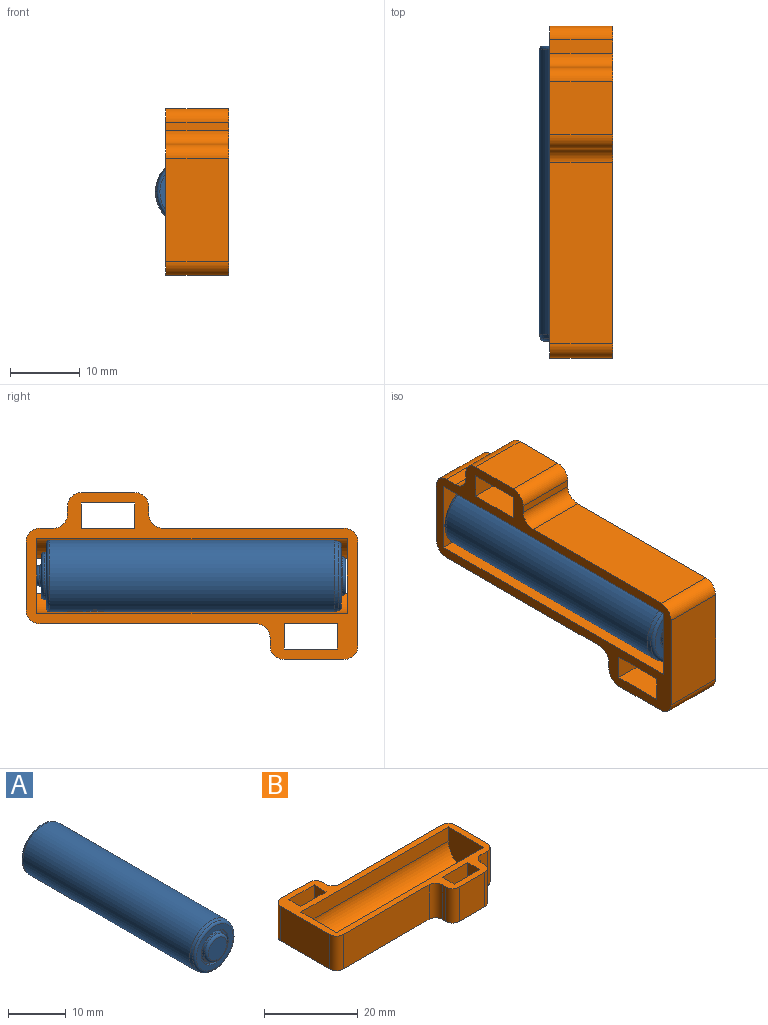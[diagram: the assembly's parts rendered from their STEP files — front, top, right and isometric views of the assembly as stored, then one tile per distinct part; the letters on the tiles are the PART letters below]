
ASSEMBLY  parts=2 mates=1
PART A: 180 faces, bbox 11.1x44.4x11.1 mm
  f0: cylinder r=4.92mm len=2.5mm, axis (0,-1,0), area 2.2mm2, adj f168,f169,f170,f171,f172,f173,f174,f175
  f1: cylinder r=4.92mm len=2.4mm, axis (0,-1,0), area 2.8mm2, adj f161,f162,f163,f164,f165,f166,f167
  f2: torus R=1.7mm, axis (0,1,0), area 3.1mm2, adj f12,f18
  f3: torus R=2.95mm, axis (0,-1,0), area 5.6mm2, adj f9,f21
  f4: torus R=1mm, axis (0,1,0), area 6.5mm2, adj f12,f19
  f5: torus R=4.62mm, axis (0,1,0), area 24.4mm2, adj f15,f16
  f6: torus R=2.9mm, axis (0,1,0), area 15.9mm2, adj f13,f18
  f7: torus R=4.48mm, axis (0,1,0), area 19.9mm2, adj f11,f20
  f8: torus R=2.25mm, axis (0,1,0), area 12.7mm2, adj f9,f22
  f9: cylinder r=2.75mm len=5.5mm, axis (0,-1,0), area 7.8mm2, adj f3,f8
  f10: cylinder r=3.35mm len=6.7mm, axis (0,-1,0), area 10.5mm2, adj f20,f21
  f11: cone r=5.12mm half-angle=14deg, axis (0,1,0), area 20.3mm2, adj f7,f15
  f12: cylinder r=1.5mm len=3mm, axis (0,-1,0), area 0.5mm2, adj f2,f4
  f13: cylinder r=3.4mm len=6.8mm, axis (0,1,0), area 9.6mm2, adj f6,f17
  f14: cylinder r=3.9mm len=7.8mm, axis (0,1,0), area 4.9mm2, adj f16,f17
  f15: cylinder r=5.12mm len=40.7mm, axis (0,-1,0), area 1276.3mm2, adj f5,f11,f23,f24,f25,f26,f27,f29
  f16: plane 9.25x9.25mm, normal (0,1,0), area 19.4mm2, adj f5,f14
  f17: plane 7.8x7.8mm, normal (0,1,0), area 11.5mm2, adj f13,f14
  f18: plane 5.8x5.8mm, normal (0,1,0), area 17.3mm2, adj f2,f6
  f19: plane 2x2mm, normal (0,1,0), area 3.1mm2, adj f4
  f20: plane 8.97x8.97mm, normal (0,-1,0), area 27.9mm2, adj f7,f10
  f21: plane 6.7x6.7mm, normal (0,-1,0), area 7.9mm2, adj f3,f10
  f22: plane 4.5x4.5mm, normal (0,-1,0), area 15.9mm2, adj f8
  f23: plane 0.64x0.19mm, normal (0.29,0,0.96), area 0.1mm2, adj f15,f24,f28,f29
  f24: bspline ~1.01x0.22mm, area 0.2mm2, adj f15,f23,f25,f28
  f25: bspline ~1.5x0.96mm, area 0.4mm2, adj f15,f24,f26,f28
  f26: bspline ~1.62x1.52mm, area 0.5mm2, adj f15,f25,f27,f28
  f27: plane 0.98x0.19mm, normal (0.32,0,-0.95), area 0.2mm2, adj f15,f26,f28,f29
  f28: cylinder r=4.92mm len=3mm, axis (0,-1,0), area 2.7mm2, adj f23,f24,f25,f26,f27,f29,f30,f31
  f29: plane 3.12x0.46mm, normal (0,-1,0), area 0.6mm2, adj f15,f23,f27,f28
  f30: bspline ~0.91x0.21mm, area 0.2mm2, adj f28,f31,f36,f37
  f31: bspline ~1.13x0.76mm, area 0.3mm2, adj f28,f30,f32,f37
  f32: bspline ~1.2x0.84mm, area 0.3mm2, adj f28,f31,f33,f37
  f33: bspline ~0.98x0.21mm, area 0.2mm2, adj f28,f32,f34,f37
  f34: plane 0.22x0.19mm, normal (-0.23,0,-0.97), area 0mm2, adj f28,f33,f35,f37
  f35: plane 2.5x0.37mm, normal (0,1,0), area 0.5mm2, adj f28,f34,f36,f37
  f36: plane 0.36x0.19mm, normal (-0.26,0,0.97), area 0.1mm2, adj f28,f30,f35,f37
  f37: cylinder r=5.12mm len=2.5mm, axis (0,-1,0), area 4.5mm2, adj f30,f31,f32,f33,f34,f35,f36
  f38: bspline ~0.99x0.69mm, area 0.3mm2, adj f15,f39,f50,f51
  f39: bspline ~1.32x0.99mm, area 0.4mm2, adj f15,f38,f40,f51
  f40: plane 1.9x0.41mm, normal (0,1,0), area 0.4mm2, adj f15,f39,f41,f51
  f41: plane 0.29x0.19mm, normal (0.29,0,0.96), area 0.1mm2, adj f15,f40,f42,f51
  f42: plane 1.88x0.41mm, normal (0,-1,0), area 0.4mm2, adj f15,f41,f43,f51
  f43: bspline ~0.5x0.26mm, area 0.1mm2, adj f15,f42,f44,f51
  f44: bspline ~0.69x0.56mm, area 0.2mm2, adj f15,f43,f45,f51
  f45: bspline ~0.74x0.62mm, area 0.2mm2, adj f15,f44,f46,f51
  f46: bspline ~0.43x0.25mm, area 0.1mm2, adj f15,f45,f47,f51
  f47: plane 1.88x0.41mm, normal (0,1,0), area 0.4mm2, adj f15,f46,f48,f51
  f48: plane 0.29x0.19mm, normal (0.29,0,0.96), area 0.1mm2, adj f15,f47,f49,f51
  f49: plane 1.9x0.41mm, normal (0,-1,0), area 0.4mm2, adj f15,f48,f50,f51
  f50: bspline ~0.68x0.29mm, area 0.1mm2, adj f15,f38,f49,f51
  f51: cylinder r=4.92mm len=3.08mm, axis (0,-1,0), area 2mm2, adj f38,f39,f40,f41,f42,f43,f44,f45
  f52: plane 1.44x0.45mm, normal (0,1,0), area 0.3mm2, adj f15,f53,f62,f63
  f53: plane 0.23x0.2mm, normal (0.04,0,-1), area 0mm2, adj f15,f52,f54,f63
  f54: bspline ~1.44x1.17mm, area 0.4mm2, adj f15,f53,f55,f63
  f55: plane 0.35x0.19mm, normal (0.32,0,-0.95), area 0.1mm2, adj f15,f54,f56,f63
  f56: bspline ~1.44x1.17mm, area 0.4mm2, adj f15,f55,f57,f63
  f57: bspline ~1.13x0.86mm, area 0.3mm2, adj f15,f56,f58,f63
  f58: bspline ~0.81x0.64mm, area 0.2mm2, adj f15,f57,f59,f63
  f59: bspline ~0.72x0.2mm, area 0.1mm2, adj f15,f58,f60,f63
  f60: plane 0.64x0.19mm, normal (0.29,0,0.96), area 0.1mm2, adj f15,f59,f61,f63
  f61: plane 3.12x0.46mm, normal (0,-1,0), area 0.6mm2, adj f15,f60,f62,f63
  f62: plane 0.29x0.19mm, normal (0.32,0,-0.95), area 0.1mm2, adj f15,f52,f61,f63
  f63: cylinder r=4.92mm len=3mm, axis (0,-1,0), area 2.5mm2, adj f52,f53,f54,f55,f56,f57,f58,f59
  f64: plane 0.58x0.2mm, normal (0.02,0.01,1), area 0.1mm2, adj f63,f65,f68,f69
  f65: bspline ~0.84x0.54mm, area 0.2mm2, adj f63,f64,f66,f69
  f66: bspline ~0.83x0.54mm, area 0.2mm2, adj f63,f65,f67,f69
  f67: plane 0.6x0.19mm, normal (-0.23,0,-0.97), area 0.1mm2, adj f63,f66,f68,f69
  f68: plane 1.05x0.33mm, normal (0,1,0), area 0.2mm2, adj f63,f64,f67,f69
  f69: cylinder r=5.12mm len=1.42mm, axis (0,-1,0), area 1.1mm2, adj f64,f65,f66,f67,f68
  f70: plane 0.31x0.19mm, normal (0.32,0,-0.95), area 0.1mm2, adj f15,f71,f77,f78
  f71: bspline ~1.02x0.47mm, area 0.2mm2, adj f15,f70,f72,f77
  f72: plane 1.44x0.2mm, normal (0.13,0,-0.99), area 0.3mm2, adj f15,f71,f73,f77
  f73: bspline ~1.02x0.48mm, area 0.2mm2, adj f15,f72,f74,f77
  f74: plane 0.31x0.19mm, normal (0.32,0,-0.95), area 0.1mm2, adj f15,f73,f75,f77
  f75: bspline ~3.12x1.51mm, area 0.7mm2, adj f15,f74,f76,f77
  f76: plane 0.19x0.06mm, normal (0.29,0,0.96), area 0mm2, adj f15,f75,f77,f78
  f77: cylinder r=4.92mm len=3.01mm, axis (0,-1,0), area 2.1mm2, adj f70,f71,f72,f73,f74,f75,f76,f78
  f78: bspline ~3.12x1.47mm, area 0.7mm2, adj f15,f70,f76,f77
  f79: plane 1.13x0.2mm, normal (-0.06,0,1), area 0.2mm2, adj f77,f80,f81,f82
  f80: bspline ~1.21x0.56mm, area 0.3mm2, adj f77,f79,f81,f82
  f81: bspline ~1.21x0.58mm, area 0.3mm2, adj f77,f79,f80,f82
  f82: cylinder r=5.12mm len=1.21mm, axis (0,-1,0), area 0.7mm2, adj f79,f80,f81
  f83: bspline ~1.15x0.55mm, area 0.3mm2, adj f15,f84,f93,f94
  f84: bspline ~1.41x1.33mm, area 0.4mm2, adj f15,f83,f85,f93
  f85: bspline ~1.43x1.33mm, area 0.4mm2, adj f15,f84,f86,f93
  f86: bspline ~1.13x0.55mm, area 0.3mm2, adj f15,f85,f87,f93
  f87: bspline ~0.25x0.23mm, area 0.1mm2, adj f15,f86,f88,f93
  f88: bspline ~1.38x0.68mm, area 0.3mm2, adj f15,f87,f89,f93
  f89: bspline ~1.31x0.58mm, area 0.3mm2, adj f15,f88,f90,f93
  f90: bspline ~1.12x0.4mm, area 0.2mm2, adj f15,f89,f91,f93
  f91: bspline ~1.71x1.63mm, area 0.5mm2, adj f15,f90,f92,f93
  f92: bspline ~1.39x0.68mm, area 0.3mm2, adj f15,f91,f93,f94
  f93: cylinder r=4.92mm len=3.15mm, axis (0,-1,0), area 2.5mm2, adj f83,f84,f85,f86,f87,f88,f89,f90
  f94: bspline ~0.25x0.23mm, area 0.1mm2, adj f15,f83,f92,f93
  f95: plane 0.36x0.28mm, normal (0,1,0), area 0.1mm2, adj f15,f96,f106,f107
  f96: plane 1.51x0.19mm, normal (-0.26,0,0.97), area 0.3mm2, adj f15,f95,f97,f107
  f97: plane 1.21x0.37mm, normal (0,1,0), area 0.2mm2, adj f15,f96,f98,f107
  f98: plane 1.51x0.2mm, normal (0.02,0,-1), area 0.3mm2, adj f15,f97,f99,f107
  f99: plane 0.33x0.2mm, normal (0,1,0), area 0.1mm2, adj f15,f98,f100,f107
  f100: plane 1.51x0.2mm, normal (0.04,0,1), area 0.3mm2, adj f15,f99,f101,f107
  f101: plane 0.97x0.33mm, normal (0,1,0), area 0.2mm2, adj f15,f100,f102,f107
  f102: plane 1.51x0.19mm, normal (-0.23,0,-0.97), area 0.3mm2, adj f15,f101,f103,f107
  f103: plane 0.36x0.28mm, normal (0,1,0), area 0.1mm2, adj f15,f102,f104,f107
  f104: plane 1.79x0.19mm, normal (0.29,0,0.96), area 0.4mm2, adj f15,f103,f105,f107
  f105: plane 3.12x0.46mm, normal (0,-1,0), area 0.6mm2, adj f15,f104,f106,f107
  f106: plane 1.79x0.19mm, normal (0.32,0,-0.95), area 0.4mm2, adj f15,f95,f105,f107
  f107: cylinder r=4.92mm len=3mm, axis (0,-1,0), area 2.3mm2, adj f95,f96,f97,f98,f99,f100,f101,f102
  f108: plane 0.36x0.28mm, normal (0,1,0), area 0.1mm2, adj f15,f109,f113,f114
  f109: plane 1.22x0.19mm, normal (-0.26,0,0.97), area 0.2mm2, adj f15,f108,f110,f114
  f110: plane 2.81x0.41mm, normal (0,1,0), area 0.6mm2, adj f15,f109,f111,f114
  f111: plane 0.29x0.19mm, normal (0.29,0,0.96), area 0.1mm2, adj f15,f110,f112,f114
  f112: plane 3.12x0.46mm, normal (0,-1,0), area 0.6mm2, adj f15,f111,f113,f114
  f113: plane 1.51x0.19mm, normal (0.32,0,-0.95), area 0.3mm2, adj f15,f108,f112,f114
  f114: cylinder r=4.92mm len=3mm, axis (0,-1,0), area 1.3mm2, adj f108,f109,f110,f111,f112,f113
  f115: plane 0.36x0.28mm, normal (0,1,0), area 0.1mm2, adj f15,f116,f120,f121
  f116: plane 1.22x0.19mm, normal (-0.26,0,0.97), area 0.2mm2, adj f15,f115,f117,f121
  f117: plane 2.81x0.41mm, normal (0,1,0), area 0.6mm2, adj f15,f116,f118,f121
  f118: plane 0.29x0.19mm, normal (0.29,0,0.96), area 0.1mm2, adj f15,f117,f119,f121
  f119: plane 3.12x0.46mm, normal (0,-1,0), area 0.6mm2, adj f15,f118,f120,f121
  f120: plane 1.51x0.19mm, normal (0.32,0,-0.95), area 0.3mm2, adj f15,f115,f119,f121
  f121: cylinder r=4.92mm len=3mm, axis (0,-1,0), area 1.3mm2, adj f115,f116,f117,f118,f119,f120
  f122: plane 0.24x0.16mm, normal (0.62,0,-0.79), area 0mm2, adj f15,f123,f129,f130
  f123: bspline ~0.76x0.6mm, area 0.2mm2, adj f15,f122,f124,f129
  f124: plane 1.13x0.17mm, normal (0.49,0,-0.87), area 0.2mm2, adj f15,f123,f125,f129
  f125: bspline ~0.76x0.6mm, area 0.2mm2, adj f15,f124,f126,f129
  f126: plane 0.25x0.16mm, normal (0.62,0,-0.79), area 0mm2, adj f15,f125,f127,f129
  f127: bspline ~2.3x1.19mm, area 0.5mm2, adj f15,f126,f128,f129
  f128: plane 0.2x0.04mm, normal (-0.18,0,0.98), area 0mm2, adj f15,f127,f129,f130
  f129: cylinder r=4.92mm len=2.37mm, axis (0,-1,0), area 1.3mm2, adj f122,f123,f124,f125,f126,f127,f128,f130
  f130: bspline ~2.3x1.17mm, area 0.5mm2, adj f15,f122,f128,f129
  f131: plane 0.89x0.18mm, normal (-0.44,0,0.9), area 0.2mm2, adj f129,f132,f133,f134
  f132: bspline ~0.95x0.52mm, area 0.2mm2, adj f129,f131,f133,f134
  f133: bspline ~0.95x0.52mm, area 0.2mm2, adj f129,f131,f132,f134
  f134: cylinder r=5.12mm len=0.89mm, axis (0,-1,0), area 0.4mm2, adj f131,f132,f133
  f135: plane 0.24x0.16mm, normal (0.62,0,-0.79), area 0mm2, adj f15,f136,f142,f143
  f136: bspline ~0.76x0.6mm, area 0.2mm2, adj f15,f135,f137,f142
  f137: plane 1.13x0.17mm, normal (0.49,0,-0.87), area 0.2mm2, adj f15,f136,f138,f142
  f138: bspline ~0.76x0.6mm, area 0.2mm2, adj f15,f137,f139,f142
  f139: plane 0.25x0.16mm, normal (0.62,0,-0.79), area 0mm2, adj f15,f138,f140,f142
  f140: bspline ~2.3x1.19mm, area 0.5mm2, adj f15,f139,f141,f142
  f141: plane 0.2x0.04mm, normal (-0.18,0,0.98), area 0mm2, adj f15,f140,f142,f143
  f142: cylinder r=4.92mm len=2.37mm, axis (0,-1,0), area 1.3mm2, adj f135,f136,f137,f138,f139,f140,f141,f143
  f143: bspline ~2.3x1.17mm, area 0.5mm2, adj f15,f135,f141,f142
  f144: plane 0.89x0.18mm, normal (-0.44,0,0.9), area 0.2mm2, adj f142,f145,f146,f147
  f145: bspline ~0.95x0.52mm, area 0.2mm2, adj f142,f144,f146,f147
  f146: bspline ~0.95x0.52mm, area 0.2mm2, adj f142,f144,f145,f147
  f147: cylinder r=5.12mm len=0.89mm, axis (0,-1,0), area 0.4mm2, adj f144,f145,f146
  f148: plane 0.24x0.16mm, normal (0.62,0,-0.79), area 0mm2, adj f15,f149,f155,f156
  f149: bspline ~0.76x0.6mm, area 0.2mm2, adj f15,f148,f150,f155
  f150: plane 1.13x0.17mm, normal (0.49,0,-0.87), area 0.2mm2, adj f15,f149,f151,f155
  f151: bspline ~0.76x0.6mm, area 0.2mm2, adj f15,f150,f152,f155
  f152: plane 0.25x0.16mm, normal (0.62,0,-0.79), area 0mm2, adj f15,f151,f153,f155
  f153: bspline ~2.3x1.19mm, area 0.5mm2, adj f15,f152,f154,f155
  f154: plane 0.2x0.04mm, normal (-0.18,0,0.98), area 0mm2, adj f15,f153,f155,f156
  f155: cylinder r=4.92mm len=2.37mm, axis (0,-1,0), area 1.3mm2, adj f148,f149,f150,f151,f152,f153,f154,f156
  f156: bspline ~2.3x1.17mm, area 0.5mm2, adj f15,f148,f154,f155
  f157: plane 0.89x0.18mm, normal (-0.44,0,0.9), area 0.2mm2, adj f155,f158,f159,f160
  f158: bspline ~0.95x0.52mm, area 0.2mm2, adj f155,f157,f159,f160
  f159: bspline ~0.95x0.52mm, area 0.2mm2, adj f155,f157,f158,f160
  f160: cylinder r=5.12mm len=0.89mm, axis (0,-1,0), area 0.4mm2, adj f157,f158,f159
  f161: plane 0.5x0.32mm, normal (0,1,0), area 0.1mm2, adj f1,f15,f162,f167
  f162: plane 1.2x0.19mm, normal (0.97,0,-0.24), area 0.2mm2, adj f1,f15,f161,f163
  f163: plane 1.29x0.34mm, normal (0,1,0), area 0.3mm2, adj f1,f15,f162,f164
  f164: plane 1.2x0.2mm, normal (-1,0,-0.01), area 0.2mm2, adj f1,f15,f163,f165
  f165: plane 0.48x0.23mm, normal (0,1,0), area 0.1mm2, adj f1,f15,f164,f166
  f166: bspline ~1.2x1.12mm, area 0.3mm2, adj f1,f15,f165,f167
  f167: bspline ~1.2x1.12mm, area 0.3mm2, adj f1,f15,f161,f166
  f168: plane 0.5x0.19mm, normal (0.94,0,-0.35), area 0.1mm2, adj f0,f15,f169,f179
  f169: plane 1x0.44mm, normal (0,1,0), area 0.2mm2, adj f0,f15,f168,f170
  f170: plane 1x0.2mm, normal (0.99,0,-0.16), area 0.2mm2, adj f0,f15,f169,f171
  f171: plane 0.51x0.25mm, normal (0,1,0), area 0.1mm2, adj f0,f15,f170,f172
  f172: plane 1x0.2mm, normal (-1,0,0.07), area 0.2mm2, adj f0,f15,f171,f173
  f173: plane 1x0.24mm, normal (0,1,0), area 0.2mm2, adj f0,f15,f172,f174
  f174: plane 0.5x0.2mm, normal (-0.99,0,-0.13), area 0.1mm2, adj f0,f15,f173,f175
  f175: plane 1x0.24mm, normal (0,-1,0), area 0.2mm2, adj f0,f15,f174,f176
  f176: plane 1x0.2mm, normal (-1,0,0.07), area 0.2mm2, adj f0,f15,f175,f177
  f177: plane 0.51x0.25mm, normal (0,-1,0), area 0.1mm2, adj f0,f15,f176,f178
  f178: plane 1x0.2mm, normal (0.99,0,-0.16), area 0.2mm2, adj f0,f15,f177,f179
  f179: plane 1x0.44mm, normal (0,-1,0), area 0.2mm2, adj f0,f15,f168,f178
PART B: 38 faces, bbox 47.5x23.9x9 mm
  f0: plane 44.5x3.65mm, normal (0,-1,0), area 162.4mm2, adj f2,f32,f33,f36
  f1: plane 44.5x3.65mm, normal (0,1,0), area 162.4mm2, adj f2,f32,f33,f34
  f2: plane 47.5x23.9mm, normal (0,0,1), area 239.6mm2, adj f0,f1,f4,f5,f6,f7,f8,f9
  f3: plane 47.5x23.9mm, normal (0,0,-1), area 493.3mm2, adj f4,f5,f6,f7,f8,f9,f10,f11
  f4: plane 9x7.65mm, normal (0,-1,0), area 68.8mm2, adj f2,f3,f14,f17
  f5: plane 9.7x9mm, normal (1,0,0), area 87.3mm2, adj f2,f3,f16,f22
  f6: plane 9x8.58mm, normal (0,1,0), area 77.2mm2, adj f2,f3,f20,f23
  f7: plane 14.8x9mm, normal (-1,0,0), area 133.2mm2, adj f2,f3,f19,f23
  f8: plane 9x1.1mm, normal (1,0,0), area 9.9mm2, adj f2,f3,f14,f15
  f9: plane 9x1.93mm, normal (0,-1,0), area 17.3mm2, adj f2,f3,f15,f16
  f10: plane 9x1.1mm, normal (-1,0,0), area 9.9mm2, adj f2,f3,f17,f18
  f11: plane 25.93x9mm, normal (0,-1,0), area 233.3mm2, adj f2,f3,f18,f19
  f12: plane 9x1.1mm, normal (1,0,0), area 9.9mm2, adj f2,f3,f20,f21
  f13: plane 30.93x9mm, normal (0,1,0), area 278.3mm2, adj f2,f3,f21,f22
  f14: cylinder r=2mm len=9mm, axis (0,0,-1), area 28.3mm2, adj f2,f3,f4,f8
  f15: cylinder r=2mm len=9mm, axis (0,0,-1), area 28.3mm2, adj f2,f3,f8,f9
  f16: cylinder r=2mm len=9mm, axis (0,0,1), area 28.3mm2, adj f2,f3,f5,f9
  f17: cylinder r=2mm len=9mm, axis (0,0,1), area 28.3mm2, adj f2,f3,f4,f10
  f18: cylinder r=2mm len=9mm, axis (0,0,-1), area 28.3mm2, adj f2,f3,f10,f11
  f19: cylinder r=2mm len=9mm, axis (0,0,1), area 28.3mm2, adj f2,f3,f7,f11
  f20: cylinder r=2mm len=9mm, axis (0,0,-1), area 28.3mm2, adj f2,f3,f6,f12
  f21: cylinder r=2mm len=9mm, axis (0,0,-1), area 28.3mm2, adj f2,f3,f12,f13
  f22: cylinder r=2mm len=9mm, axis (0,0,-1), area 28.3mm2, adj f2,f3,f5,f13
  f23: cylinder r=2mm len=9mm, axis (0,0,1), area 28.3mm2, adj f2,f3,f6,f7
  f24: plane 9x3.6mm, normal (1,0,0), area 32.4mm2, adj f2,f3,f25,f27
  f25: plane 9x7.65mm, normal (0,-1,0), area 68.8mm2, adj f2,f3,f24,f26
  f26: plane 9x3.6mm, normal (-1,0,0), area 32.4mm2, adj f2,f3,f25,f27
  f27: plane 9x7.65mm, normal (0,1,0), area 68.8mm2, adj f2,f3,f24,f26
  f28: plane 9x3.6mm, normal (1,0,0), area 32.4mm2, adj f2,f3,f29,f31
  f29: plane 9x7.65mm, normal (0,-1,0), area 68.8mm2, adj f2,f3,f28,f30
  f30: plane 9x3.6mm, normal (-1,0,0), area 32.4mm2, adj f2,f3,f29,f31
  f31: plane 9x7.65mm, normal (0,1,0), area 68.8mm2, adj f2,f3,f28,f30
  f32: plane 10.7x9mm, normal (-1,0,0), area 85mm2, adj f0,f1,f2,f3,f34,f35,f36,f37
  f33: plane 10.7x9mm, normal (1,0,0), area 85mm2, adj f0,f1,f2,f3,f34,f35,f36,f37
  f34: cylinder r=5.35mm len=44.5mm, axis (-1,0,0), area 258.2mm2, adj f1,f32,f33,f35
  f35: plane 44.5x0.62mm, normal (0,1,0), area 27.6mm2, adj f3,f32,f33,f34
  f36: cylinder r=5.35mm len=44.5mm, axis (-1,0,0), area 258.2mm2, adj f0,f32,f33,f37
  f37: plane 44.5x0.62mm, normal (0,-1,0), area 27.6mm2, adj f3,f32,f33,f36
PLACE A t=(34.04,26.86,12.13)mm
PLACE B rot(axis=(-0.58,-0.58,0.58),120deg) t=(39.39,48.21,12.13)mm
MATE parallel B.f36 <-> A.f0  axis (0,-1,0) through (34.04,48.21,12.13)mm
